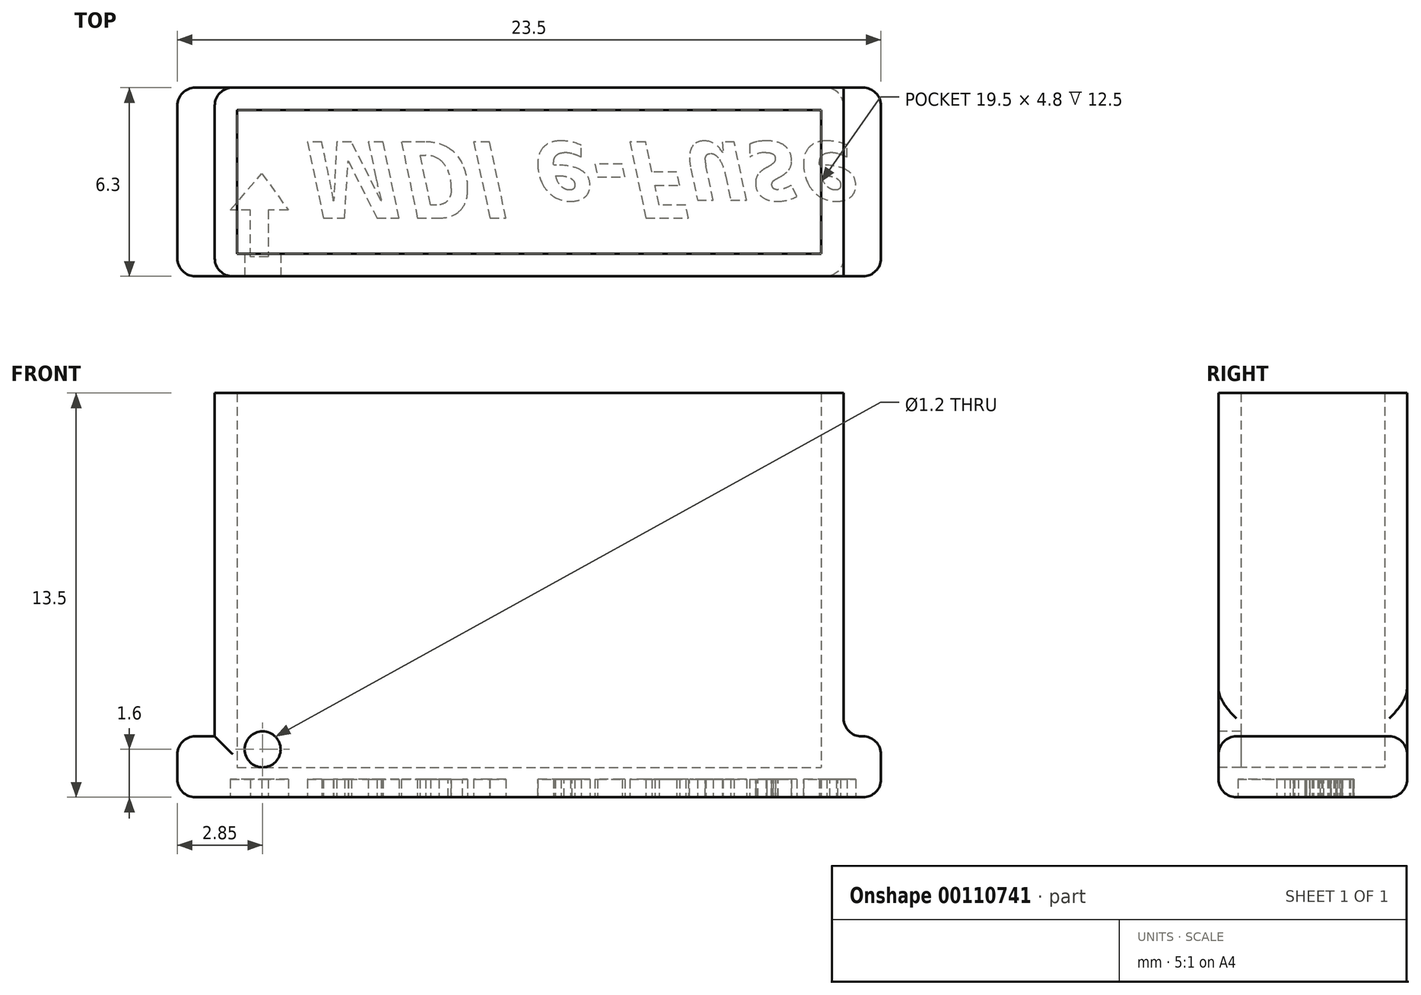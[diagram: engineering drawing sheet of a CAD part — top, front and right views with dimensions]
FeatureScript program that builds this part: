
annotation { "Feature Type Name" : "Feature", "Feature Type Description" : "" }
export const myFeature = defineFeature(function(context is Context, id is Id, definition is map)
    precondition{}
    {
        {
            var Q0;
            Q0=qCreatedBy(makeId("Top.planeOp"),FACE);
            var sketch = newSketch(context, id + "F0", { "sketchPlane" : qUnion([Q0])});
            skLineSegment(sketch, "E0.bottom", {"start": v(-9.75, 2.4) * mm, "end": v(9.75, 2.4) * mm});
            skLineSegment(sketch, "E0.top", {"start": v(-9.75, -2.4) * mm, "end": v(9.75, -2.4) * mm});
            skLineSegment(sketch, "E0.left", {"start": v(-9.75, 2.4) * mm, "end": v(-9.75, -2.4) * mm});
            skLineSegment(sketch, "E0.right", {"start": v(9.75, 2.4) * mm, "end": v(9.75, -2.4) * mm});
            skPoint(sketch, "E0.middle", {"position": v(0, 0) * mm});
            skLineSegment(sketch, "E1.bottom", {"start": v(-10.5, 3.15) * mm, "end": v(10.5, 3.15) * mm});
            skLineSegment(sketch, "E1.top", {"start": v(-10.5, -3.15) * mm, "end": v(10.5, -3.15) * mm});
            skLineSegment(sketch, "E1.left", {"start": v(-10.5, 3.15) * mm, "end": v(-10.5, -3.15) * mm});
            skLineSegment(sketch, "E1.right", {"start": v(10.5, 3.15) * mm, "end": v(10.5, -3.15) * mm});
            skLineSegment(sketch, "E2.bottom", {"start": v(-11.75, 3.15) * mm, "end": v(11.75, 3.15) * mm});
            skLineSegment(sketch, "E2.top", {"start": v(-11.75, -3.15) * mm, "end": v(11.75, -3.15) * mm});
            skLineSegment(sketch, "E2.left", {"start": v(-11.75, 3.15) * mm, "end": v(-11.75, -3.15) * mm});
            skLineSegment(sketch, "E2.right", {"start": v(11.75, 3.15) * mm, "end": v(11.75, -3.15) * mm});
            skSolve(sketch);
        }
        {
            var Q0;
            Q0=makeQuery(id+"F0.imprint","IMPRINT",FACE,{"disambiguationData":[TD([[makeQuery(id+"F0.imprint","IMPRINT",EDGE,{"derivedFrom":sQuery(id+"F0.wireOp",EDGE,"E0.bottom")}),-1.0]])]});
            extrude(context, id + "F1", {"entities" : qUnion([Q0]), "depth" : 1 * mm});
        }
        {
            var Q0;
            Q0=makeQuery(id+"F0.imprint","IMPRINT",FACE,{"disambiguationData":[TD([[makeQuery(id+"F0.imprint","IMPRINT",EDGE,{"derivedFrom":sQuery(id+"F0.wireOp",EDGE,"E0.bottom")}),1.0]])]});
            extrude(context, id + "F2", {"entities" : qUnion([Q0]), "operationType" : NewBodyOperationType.ADD, "depth" : 13.5 * mm});
        }
        {
            var Q0;
            {var subQ0=sQuery(id+"F0.wireOp",EDGE,"E1.left");Q0=makeQuery(id+"F0.imprint","IMPRINT",FACE,{"disambiguationData":[TD([[makeQuery(id+"F0.imprint","IMPRINT",EDGE,{"derivedFrom":subQ0}),-1.0]])]});}
            var Q1;
            {var subQ0=sQuery(id+"F0.wireOp",EDGE,"E1.right");Q1=makeQuery(id+"F0.imprint","IMPRINT",FACE,{"disambiguationData":[TD([[makeQuery(id+"F0.imprint","IMPRINT",EDGE,{"derivedFrom":subQ0}),1.0]])]});}
            extrude(context, id + "F3", {"entities" : qUnion([Q0, Q1]), "operationType" : NewBodyOperationType.ADD, "depth" : 2.03 * mm});
        }
        {
            var Q0;
            Q0=makeQuery(id+"F3.opExtrude","CAP_EDGE",EDGE,{"disambiguationData":[OSD([sQuery(id+"F0.wireOp",EDGE,"E2.left")])],"isStart":false});
            var Q1;
            Q1=makeQuery(id+"F3.opExtrude","CAP_EDGE",EDGE,{"disambiguationData":[OSD([sQuery(id+"F0.wireOp",EDGE,"E2.right")])],"isStart":false});
            var Q2;
            Q2=makeQuery(id+"F3.opExtrude","SWEPT_EDGE",EDGE,{"disambiguationData":[OSD([sQuery(id+"F0.wireOp",EDGE,"E2.top"),sQuery(id+"F0.wireOp",EDGE,"E2.right")])]});
            var Q3;
            Q3=makeQuery(id+"F3.opExtrude","CAP_FACE",FACE,{"disambiguationData":[OSD([sQuery(id+"F0.wireOp",EDGE,"E1.right"),sQuery(id+"F0.wireOp",EDGE,"E2.bottom"),sQuery(id+"F0.wireOp",EDGE,"E2.top"),sQuery(id+"F0.wireOp",EDGE,"E2.right")])],"isStart":false});
            var Q4;
            {var subQ0=sQuery(id+"F0.wireOp",EDGE,"E2.top");Q4=makeQuery(id+"F3.opExtrude","CAP_EDGE",EDGE,{"disambiguationData":[OSD([subQ0]),TDD([makeQuery(id+"F0.imprint","IMPRINT",EDGE,{"disambiguationData":[TD([[makeQuery(id+"F0.imprint","INTERSECT",VERTEX,{"derivedFrom":[sQuery(id+"F0.wireOp",EDGE,"E1.left"),subQ0]}),1.0]])],"derivedFrom":subQ0})])],"isStart":false});}
            var Q5;
            Q5=makeQuery(id+"F2.opExtrude","SWEPT_EDGE",EDGE,{"disambiguationData":[OSD([sQuery(id+"F0.wireOp",EDGE,"E1.left"),sQuery(id+"F0.wireOp",EDGE,"E2.top")])]});
            var Q6;
            {var subQ0=sQuery(id+"F0.wireOp",EDGE,"E2.bottom");Q6=makeQuery(id+"F3.opExtrude","CAP_EDGE",EDGE,{"disambiguationData":[OSD([subQ0]),TDD([makeQuery(id+"F0.imprint","IMPRINT",EDGE,{"disambiguationData":[TD([[makeQuery(id+"F0.imprint","INTERSECT",VERTEX,{"derivedFrom":[sQuery(id+"F0.wireOp",EDGE,"E1.left"),subQ0]}),1.0]])],"derivedFrom":subQ0})])],"isStart":false});}
            var Q7;
            Q7=makeQuery(id+"F2.opExtrude","SWEPT_EDGE",EDGE,{"disambiguationData":[OSD([sQuery(id+"F0.wireOp",EDGE,"E1.left"),sQuery(id+"F0.wireOp",EDGE,"E2.bottom")])]});
            var Q8;
            Q8=makeQuery(id+"F3.opExtrude","SWEPT_EDGE",EDGE,{"disambiguationData":[OSD([sQuery(id+"F0.wireOp",EDGE,"E2.bottom"),sQuery(id+"F0.wireOp",EDGE,"E2.left")])]});
            var Q9;
            Q9=makeQuery(id+"F3.opExtrude","SWEPT_EDGE",EDGE,{"disambiguationData":[OSD([sQuery(id+"F0.wireOp",EDGE,"E2.top"),sQuery(id+"F0.wireOp",EDGE,"E2.left")])]});
            var Q10;
            {var subQ0=sQuery(id+"F0.wireOp",EDGE,"E2.bottom");Q10=makeQuery(id+"F3.boolean.opBoolean","MERGE",EDGE,{"derivedFrom":[makeQuery(id+"F2.opExtrude","CAP_EDGE",EDGE,{"disambiguationData":[OSD([subQ0])],"isStart":true}),makeQuery(id+"F3.opExtrude","CAP_EDGE",EDGE,{"disambiguationData":[OSD([subQ0]),TDD([makeQuery(id+"F0.imprint","IMPRINT",EDGE,{"disambiguationData":[TD([[makeQuery(id+"F0.imprint","INTERSECT",VERTEX,{"derivedFrom":[sQuery(id+"F0.wireOp",EDGE,"E1.left"),subQ0]}),1.0]])],"derivedFrom":subQ0})])],"isStart":true}),makeQuery(id+"F3.opExtrude","CAP_EDGE",EDGE,{"disambiguationData":[OSD([subQ0]),TDD([makeQuery(id+"F0.imprint","IMPRINT",EDGE,{"disambiguationData":[TD([[makeQuery(id+"F0.imprint","INTERSECT",VERTEX,{"derivedFrom":[sQuery(id+"F0.wireOp",EDGE,"E1.right"),subQ0]}),-1.0]])],"derivedFrom":subQ0})])],"isStart":true})]});}
            var Q11;
            {var subQ0=sQuery(id+"F0.wireOp",EDGE,"E2.top");Q11=makeQuery(id+"F3.boolean.opBoolean","MERGE",EDGE,{"derivedFrom":[makeQuery(id+"F2.opExtrude","CAP_EDGE",EDGE,{"disambiguationData":[OSD([subQ0])],"isStart":true}),makeQuery(id+"F3.opExtrude","CAP_EDGE",EDGE,{"disambiguationData":[OSD([subQ0]),TDD([makeQuery(id+"F0.imprint","IMPRINT",EDGE,{"disambiguationData":[TD([[makeQuery(id+"F0.imprint","INTERSECT",VERTEX,{"derivedFrom":[sQuery(id+"F0.wireOp",EDGE,"E1.left"),subQ0]}),1.0]])],"derivedFrom":subQ0})])],"isStart":true}),makeQuery(id+"F3.opExtrude","CAP_EDGE",EDGE,{"disambiguationData":[OSD([subQ0]),TDD([makeQuery(id+"F0.imprint","IMPRINT",EDGE,{"disambiguationData":[TD([[makeQuery(id+"F0.imprint","INTERSECT",VERTEX,{"derivedFrom":[sQuery(id+"F0.wireOp",EDGE,"E1.right"),subQ0]}),-1.0]])],"derivedFrom":subQ0})])],"isStart":true})]});}
            var Q12;
            Q12=makeQuery(id+"F3.opExtrude","CAP_EDGE",EDGE,{"disambiguationData":[OSD([sQuery(id+"F0.wireOp",EDGE,"E2.right")])],"isStart":true});
            var Q13;
            Q13=makeQuery(id+"F3.opExtrude","CAP_EDGE",EDGE,{"disambiguationData":[OSD([sQuery(id+"F0.wireOp",EDGE,"E2.left")])],"isStart":true});
            var Q14;
            Q14=makeQuery(id+"F3.opExtrude","SWEPT_EDGE",EDGE,{"disambiguationData":[OSD([sQuery(id+"F0.wireOp",EDGE,"E2.bottom"),sQuery(id+"F0.wireOp",EDGE,"E2.right")])]});
            fillet(context, id + "F4", {"entities" : qUnion([Q0, Q1, Q2, Q3, Q4, Q5, Q6, Q7, Q8, Q9, Q10, Q11, Q12, Q13, Q14]), "radius" : .6 * mm, "tangentPropagation" : true, "allowEdgeOverflow" : false});
        }
        {
            var Q0;
            {var subQ0=sQuery(id+"F0.wireOp",EDGE,"E2.top");Q0=makeQuery(id+"F3.boolean.opBoolean","MERGE",FACE,{"derivedFrom":[makeQuery(id+"F2.opExtrude","SWEPT_FACE",FACE,{"disambiguationData":[OSD([subQ0])]}),makeQuery(id+"F3.opExtrude","SWEPT_FACE",FACE,{"disambiguationData":[OSD([subQ0]),TDD([makeQuery(id+"F0.imprint","IMPRINT",EDGE,{"disambiguationData":[TD([[makeQuery(id+"F0.imprint","INTERSECT",VERTEX,{"derivedFrom":[sQuery(id+"F0.wireOp",EDGE,"E1.left"),subQ0]}),1.0]])],"derivedFrom":subQ0})])]}),makeQuery(id+"F3.opExtrude","SWEPT_FACE",FACE,{"disambiguationData":[OSD([subQ0]),TDD([makeQuery(id+"F0.imprint","IMPRINT",EDGE,{"disambiguationData":[TD([[makeQuery(id+"F0.imprint","INTERSECT",VERTEX,{"derivedFrom":[sQuery(id+"F0.wireOp",EDGE,"E1.right"),subQ0]}),-1.0]])],"derivedFrom":subQ0})])]})]});}
            var sketch = newSketch(context, id + "F5", { "sketchPlane" : qUnion([Q0])});
            skCircle(sketch, "E3", {"center": v(-8.9, 1.6) * mm, "radius": 0.6 * mm});
            skSolve(sketch);
        }
        {
            var Q0;
            Q0 = qSketchRegion(id + "F5", true);
            extrude(context, id + "F6", {"entities" : qUnion([Q0]), "operationType" : NewBodyOperationType.REMOVE, "oppositeDirection" : true, "depth" : 2 * mm});
        }
        {
            var Q0;
            {var subQ0=sQuery(id+"F0.wireOp",EDGE,"E2.top");var subQ1=sQuery(id+"F0.wireOp",EDGE,"E2.bottom");var subQ2=sQuery(id+"F0.wireOp",EDGE,"E1.right");var subQ3=sQuery(id+"F0.wireOp",EDGE,"E1.left");var subQ4=sQuery(id+"F0.wireOp",EDGE,"E0.right");var subQ5=sQuery(id+"F0.wireOp",EDGE,"E0.left");var subQ6=sQuery(id+"F0.wireOp",EDGE,"E0.top");var subQ7=sQuery(id+"F0.wireOp",EDGE,"E0.bottom");Q0=makeQuery(id+"F3.boolean.opBoolean","MERGE",FACE,{"derivedFrom":[makeQuery(id+"F2.boolean.opBoolean","MERGE",FACE,{"derivedFrom":[makeQuery(id+"F1.opExtrude","CAP_FACE",FACE,{"disambiguationData":[OSD([subQ7,subQ6,subQ5,subQ4])],"isStart":true}),makeQuery(id+"F2.opExtrude","CAP_FACE",FACE,{"disambiguationData":[OSD([subQ7,subQ6,subQ5,subQ4,subQ3,subQ2,subQ1,subQ0])],"isStart":true})]}),makeQuery(id+"F3.opExtrude","CAP_FACE",FACE,{"disambiguationData":[OSD([subQ3,subQ1,subQ0,sQuery(id+"F0.wireOp",EDGE,"E2.left")])],"isStart":true}),makeQuery(id+"F3.opExtrude","CAP_FACE",FACE,{"disambiguationData":[OSD([subQ2,subQ1,subQ0,sQuery(id+"F0.wireOp",EDGE,"E2.right")])],"isStart":true})]});}
            var sketch = newSketch(context, id + "F7", { "sketchPlane" : qUnion([Q0])});
            skText(sketch, "E4", { "text": "MDI e-Fuse", "fontName": "OpenSans-BoldItalic.ttf"});
            skLineSegment(sketch, "E5", {"start": v(-9.98, 0.94) * mm, "end": v(-8.92, -0.29) * mm});
            skLineSegment(sketch, "E6", {"start": v(-8.92, -0.29) * mm, "end": v(-8.04, 0.94) * mm});
            skLineSegment(sketch, "E7", {"start": v(-8.04, 0.94) * mm, "end": v(-8.71, 0.94) * mm});
            skLineSegment(sketch, "E8", {"start": v(-8.71, 0.94) * mm, "end": v(-8.71, 2.5) * mm});
            skLineSegment(sketch, "E9", {"start": v(-8.71, 2.5) * mm, "end": v(-9.31, 2.5) * mm});
            skLineSegment(sketch, "E10", {"start": v(-9.31, 2.5) * mm, "end": v(-9.31, 0.94) * mm});
            skLineSegment(sketch, "E11", {"start": v(-9.31, 0.94) * mm, "end": v(-9.98, 0.94) * mm});
            const initialGuessF7  = {"E4": [-0.0075, -0.00134, 1, 0, 0.00257]};
            skSetInitialGuess(sketch, initialGuessF7);
            skSolve(sketch);
        }
        {
            var Q0;
            Q0 = qSketchRegion(id + "F7", true);
            extrude(context, id + "F8", {"entities" : qUnion([Q0]), "operationType" : NewBodyOperationType.REMOVE, "oppositeDirection" : true, "depth" : .6 * mm});
        }
    });
